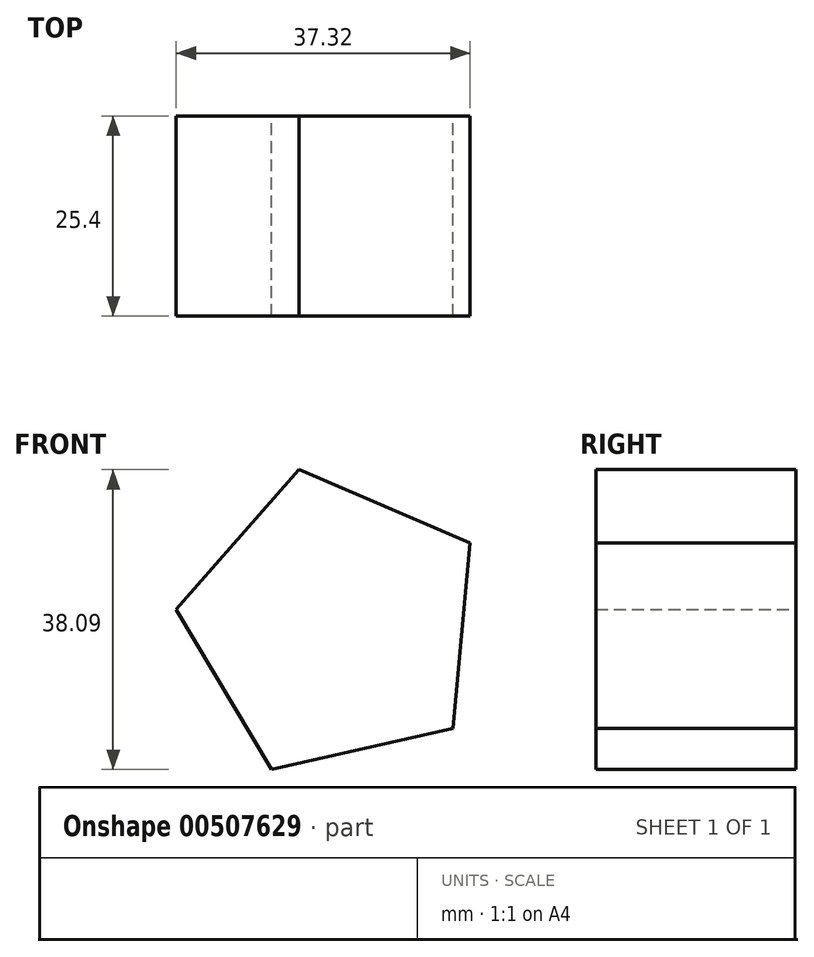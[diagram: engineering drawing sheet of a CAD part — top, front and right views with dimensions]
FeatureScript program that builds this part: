
annotation { "Feature Type Name" : "Feature", "Feature Type Description" : "" }
export const myFeature = defineFeature(function(context is Context, id is Id, definition is map)
    precondition{}
    {
        {
            var Q0;
            Q0=qCreatedBy(makeId("Front.planeOp"),FACE);
            var sketch = newSketch(context, id + "F0", { "sketchPlane" : qUnion([Q0])});
            skCircle(sketch, "E0.cCircle", {"center": v(0, 0) * mm, "radius": 16.27 * mm, "construction": true});
            skLineSegment(sketch, "E0.0", {"start": v(-7.96, -18.47) * mm, "end": v(-20.03, 1.86) * mm});
            skLineSegment(sketch, "E0.1", {"start": v(-20.03, 1.86) * mm, "end": v(-4.42, 19.62) * mm});
            skLineSegment(sketch, "E0.2", {"start": v(-4.42, 19.62) * mm, "end": v(17.3, 10.27) * mm});
            skLineSegment(sketch, "E0.3", {"start": v(17.3, 10.27) * mm, "end": v(15.1, -13.27) * mm});
            skLineSegment(sketch, "E0.4", {"start": v(15.1, -13.27) * mm, "end": v(-7.96, -18.47) * mm});
            skPoint(sketch, "E0.0.midPoint", {"position": v(-14, -8.3) * mm});
            skSolve(sketch);
        }
        {
            var Q0;
            Q0=makeQuery(id+"F0.imprint","IMPRINT",FACE,{"disambiguationData":[TD([[makeQuery(id+"F0.imprint","IMPRINT",EDGE,{"derivedFrom":sQuery(id+"F0.wireOp",EDGE,"E0.0")}),-1.0]])]});
            extrude(context, id + "F1", {"entities" : qUnion([Q0]), "endBound" : BoundingType.SYMMETRIC, "depth" : 25.4 * mm});
        }
    });
